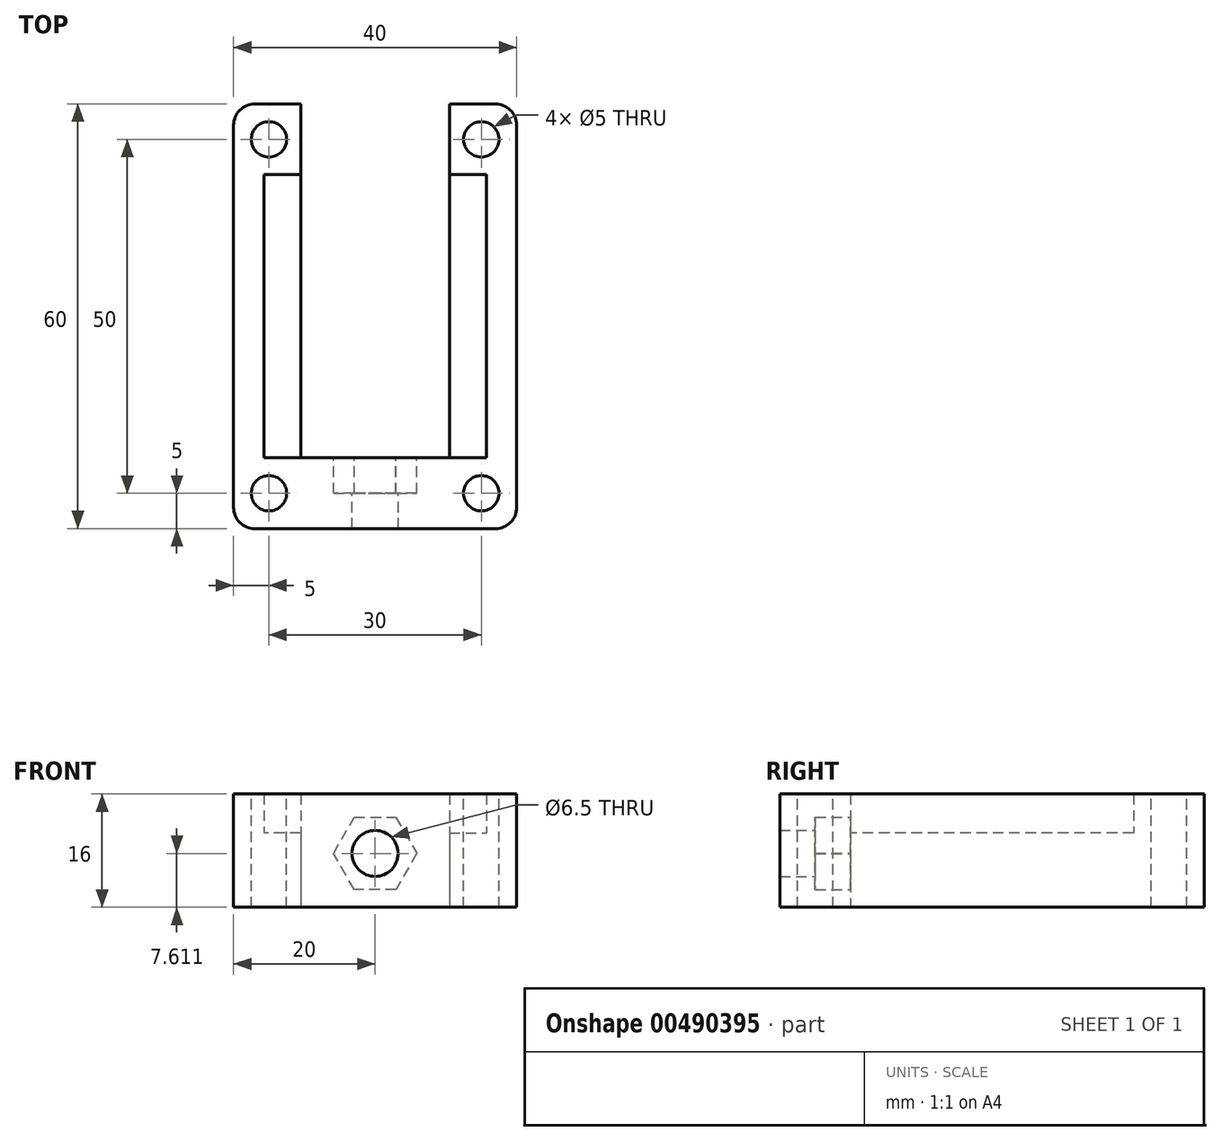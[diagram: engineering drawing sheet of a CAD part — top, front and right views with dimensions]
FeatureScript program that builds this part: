
annotation { "Feature Type Name" : "Feature", "Feature Type Description" : "" }
export const myFeature = defineFeature(function(context is Context, id is Id, definition is map)
    precondition{}
    {
        {
            var Q0;
            Q0=qCreatedBy(makeId("Top.planeOp"),FACE);
            var sketch = newSketch(context, id + "F0", { "sketchPlane" : qUnion([Q0])});
            skLineSegment(sketch, "E0.bottom", {"start": v(20, -30) * mm, "end": v(-20, -30) * mm});
            skLineSegment(sketch, "E0.top", {"start": v(20, 30) * mm, "end": v(-20, 30) * mm});
            skLineSegment(sketch, "E0.left", {"start": v(20, -30) * mm, "end": v(20, 30) * mm});
            skLineSegment(sketch, "E0.right", {"start": v(-20, -30) * mm, "end": v(-20, 30) * mm});
            skPoint(sketch, "E0.middle", {"position": v(0, 0) * mm});
            skLineSegment(sketch, "E1.bottom", {"start": v(10.5, -20) * mm, "end": v(-10.5, -20) * mm});
            skLineSegment(sketch, "E1.top", {"start": v(10.5, 20) * mm, "end": v(-10.5, 20) * mm});
            skLineSegment(sketch, "E1.left", {"start": v(10.5, -20) * mm, "end": v(10.5, 20) * mm});
            skLineSegment(sketch, "E1.right", {"start": v(-10.5, -20) * mm, "end": v(-10.5, 20) * mm});
            skLineSegment(sketch, "E2.bottom", {"start": v(-10.5, 30) * mm, "end": v(-15.7, 30) * mm});
            skLineSegment(sketch, "E2.top", {"start": v(-10.5, -30) * mm, "end": v(-15.7, -30) * mm});
            skLineSegment(sketch, "E2.left", {"start": v(-10.5, 30) * mm, "end": v(-10.5, -30) * mm});
            skLineSegment(sketch, "E2.right", {"start": v(-15.7, 30) * mm, "end": v(-15.7, -30) * mm});
            skLineSegment(sketch, "E3.bottom", {"start": v(10.5, 30) * mm, "end": v(15.7, 30) * mm});
            skLineSegment(sketch, "E3.top", {"start": v(10.5, -30) * mm, "end": v(15.7, -30) * mm});
            skLineSegment(sketch, "E3.left", {"start": v(10.5, 30) * mm, "end": v(10.5, -30) * mm});
            skLineSegment(sketch, "E3.right", {"start": v(15.7, 30) * mm, "end": v(15.7, -30) * mm});
            skLineSegment(sketch, "E4", {"start": v(-10.5, 20) * mm, "end": v(-15.7, 20) * mm});
            skLineSegment(sketch, "E5", {"start": v(-15.7, 20) * mm, "end": v(15.7, 20) * mm});
            skLineSegment(sketch, "E6", {"start": v(10.5, -20) * mm, "end": v(15.7, -20) * mm});
            skLineSegment(sketch, "E7", {"start": v(-10.5, -20) * mm, "end": v(-15.7, -20) * mm});
            skLineSegment(sketch, "E8.bottom", {"start": v(-20, -30) * mm, "end": v(-10, -30) * mm});
            skLineSegment(sketch, "E8.top", {"start": v(-20, -40) * mm, "end": v(-10, -40) * mm});
            skLineSegment(sketch, "E8.left", {"start": v(-20, -30) * mm, "end": v(-20, -40) * mm});
            skLineSegment(sketch, "E8.right", {"start": v(-10, -30) * mm, "end": v(-10, -40) * mm});
            skLineSegment(sketch, "E9.bottom", {"start": v(20, -30) * mm, "end": v(10, -30) * mm});
            skLineSegment(sketch, "E9.top", {"start": v(20, -40) * mm, "end": v(10, -40) * mm});
            skLineSegment(sketch, "E9.left", {"start": v(20, -30) * mm, "end": v(20, -40) * mm});
            skLineSegment(sketch, "E9.right", {"start": v(10, -30) * mm, "end": v(10, -40) * mm});
            skLineSegment(sketch, "E10.bottom", {"start": v(-20, 30) * mm, "end": v(-10, 30) * mm});
            skLineSegment(sketch, "E10.top", {"start": v(-20, 40) * mm, "end": v(-10, 40) * mm});
            skLineSegment(sketch, "E10.left", {"start": v(-20, 30) * mm, "end": v(-20, 40) * mm});
            skLineSegment(sketch, "E10.right", {"start": v(-10, 30) * mm, "end": v(-10, 40) * mm});
            skLineSegment(sketch, "E11.bottom", {"start": v(20, 30) * mm, "end": v(10, 30) * mm});
            skLineSegment(sketch, "E11.top", {"start": v(20, 40) * mm, "end": v(10, 40) * mm});
            skLineSegment(sketch, "E11.left", {"start": v(20, 30) * mm, "end": v(20, 40) * mm});
            skLineSegment(sketch, "E11.right", {"start": v(10, 30) * mm, "end": v(10, 40) * mm});
            skSolve(sketch);
        }
        {
            var Q0;
            {var subQ0=sQuery(id+"F0.wireOp",EDGE,"E2.bottom");Q0=makeQuery(id+"F0.imprint","IMPRINT",FACE,{"disambiguationData":[TD([[makeQuery(id+"F0.imprint","IMPRINT",EDGE,{"derivedFrom":subQ0}),1.0]])]});}
            var Q1;
            {var subQ4=sQuery(id+"F0.wireOp",EDGE,"E0.right");Q1=makeQuery(id+"F0.imprint","IMPRINT",FACE,{"disambiguationData":[TD([[makeQuery(id+"F0.imprint","IMPRINT",EDGE,{"derivedFrom":subQ4}),-1.0]])]});}
            var Q2;
            {var subQ0=sQuery(id+"F0.wireOp",EDGE,"E2.top");Q2=makeQuery(id+"F0.imprint","IMPRINT",FACE,{"disambiguationData":[TD([[makeQuery(id+"F0.imprint","IMPRINT",EDGE,{"derivedFrom":subQ0}),-1.0]])]});}
            var Q3;
            {var subQ5=sQuery(id+"F0.wireOp",EDGE,"E1.bottom");Q3=makeQuery(id+"F0.imprint","IMPRINT",FACE,{"disambiguationData":[TD([[makeQuery(id+"F0.imprint","IMPRINT",EDGE,{"derivedFrom":subQ5}),1.0]])]});}
            var Q4;
            {var subQ0=sQuery(id+"F0.wireOp",EDGE,"E3.top");Q4=makeQuery(id+"F0.imprint","IMPRINT",FACE,{"disambiguationData":[TD([[makeQuery(id+"F0.imprint","IMPRINT",EDGE,{"derivedFrom":subQ0}),1.0]])]});}
            var Q5;
            {var subQ4=sQuery(id+"F0.wireOp",EDGE,"E0.left");Q5=makeQuery(id+"F0.imprint","IMPRINT",FACE,{"disambiguationData":[TD([[makeQuery(id+"F0.imprint","IMPRINT",EDGE,{"derivedFrom":subQ4}),1.0]])]});}
            var Q6;
            {var subQ0=sQuery(id+"F0.wireOp",EDGE,"E3.bottom");Q6=makeQuery(id+"F0.imprint","IMPRINT",FACE,{"disambiguationData":[TD([[makeQuery(id+"F0.imprint","IMPRINT",EDGE,{"derivedFrom":subQ0}),-1.0]])]});}
            var Q7;
            {var subQ0=sQuery(id+"F0.wireOp",EDGE,"E2.left");var subQ5=sQuery(id+"F0.wireOp",EDGE,"E5");var subQ7=makeQuery(id+"F0.imprint","INTERSECT",VERTEX,{"derivedFrom":[subQ0,subQ5]});Q7=makeQuery(id+"F0.imprint","IMPRINT",FACE,{"disambiguationData":[TD([[makeQuery(id+"F0.imprint","IMPRINT",EDGE,{"disambiguationData":[TD([[subQ7,-1.0]])],"derivedFrom":subQ5}),1.0]])]});}
            var Q8;
            {var subQ0=sQuery(id+"F0.wireOp",EDGE,"E6");Q8=makeQuery(id+"F0.imprint","IMPRINT",FACE,{"disambiguationData":[TD([[makeQuery(id+"F0.imprint","IMPRINT",EDGE,{"derivedFrom":subQ0}),-1.0]])]});}
            var Q9;
            {var subQ0=sQuery(id+"F0.wireOp",EDGE,"E7");Q9=makeQuery(id+"F0.imprint","IMPRINT",FACE,{"disambiguationData":[TD([[makeQuery(id+"F0.imprint","IMPRINT",EDGE,{"derivedFrom":subQ0}),1.0]])]});}
            var Q10;
            {var subQ0=sQuery(id+"F0.wireOp",EDGE,"E10.bottom");var subQ1=sQuery(id+"F0.wireOp",EDGE,"E2.left");var subQ2=makeQuery(id+"F0.imprint","INTERSECT",VERTEX,{"derivedFrom":[subQ1,subQ0]});Q10=makeQuery(id+"F0.imprint","IMPRINT",FACE,{"disambiguationData":[TD([[makeQuery(id+"F0.imprint","IMPRINT",EDGE,{"disambiguationData":[TD([[subQ2,-1.0]])],"derivedFrom":subQ1}),-1.0]])]});}
            var Q11;
            {var subQ0=sQuery(id+"F0.wireOp",EDGE,"E11.bottom");var subQ1=sQuery(id+"F0.wireOp",EDGE,"E3.left");var subQ2=makeQuery(id+"F0.imprint","INTERSECT",VERTEX,{"derivedFrom":[subQ1,subQ0]});Q11=makeQuery(id+"F0.imprint","IMPRINT",FACE,{"disambiguationData":[TD([[makeQuery(id+"F0.imprint","IMPRINT",EDGE,{"disambiguationData":[TD([[subQ2,-1.0]])],"derivedFrom":subQ1}),1.0]])]});}
            extrude(context, id + "F1", {"entities" : qUnion([Q0, Q1, Q2, Q3, Q4, Q5, Q6, Q7, Q8, Q9, Q10, Q11]), "depth" : 16 * mm});
        }
        {
            var Q0;
            {var subQ0=sQuery(id+"F0.wireOp",EDGE,"E7");Q0=makeQuery(id+"F0.imprint","IMPRINT",FACE,{"disambiguationData":[TD([[makeQuery(id+"F0.imprint","IMPRINT",EDGE,{"derivedFrom":subQ0}),-1.0]])]});}
            var Q1;
            {var subQ0=sQuery(id+"F0.wireOp",EDGE,"E6");Q1=makeQuery(id+"F0.imprint","IMPRINT",FACE,{"disambiguationData":[TD([[makeQuery(id+"F0.imprint","IMPRINT",EDGE,{"derivedFrom":subQ0}),1.0]])]});}
            extrude(context, id + "F2", {"entities" : qUnion([Q0, Q1]), "operationType" : NewBodyOperationType.ADD, "depth" : 10.5 * mm});
        }
        {
            var Q0;
            Q0=makeQuery(id+"F1.opExtrude","SWEPT_FACE",FACE,{"disambiguationData":[OSD([sQuery(id+"F0.wireOp",EDGE,"E1.bottom"),sQuery(id+"F0.wireOp",EDGE,"E6"),sQuery(id+"F0.wireOp",EDGE,"E7")])]});
            var sketch = newSketch(context, id + "F3", { "sketchPlane" : qUnion([Q0])});
            skCircle(sketch, "E12", {"center": v(0, 7.61) * mm, "radius": 3.25 * mm});
            skPoint(sketch, "E12.centerSnap0", {"position": v(0, 16) * mm});
            skCircle(sketch, "E13.cCircle", {"center": v(0, 7.61) * mm, "radius": 5.1 * mm, "construction": true});
            skLineSegment(sketch, "E13.0", {"start": v(-5.89, 7.63) * mm, "end": v(-2.93, 12.72) * mm});
            skLineSegment(sketch, "E13.1", {"start": v(-2.93, 12.72) * mm, "end": v(2.96, 12.7) * mm});
            skLineSegment(sketch, "E13.2", {"start": v(2.96, 12.7) * mm, "end": v(5.89, 7.6) * mm});
            skLineSegment(sketch, "E13.3", {"start": v(5.89, 7.6) * mm, "end": v(2.93, 2.5) * mm});
            skLineSegment(sketch, "E13.4", {"start": v(2.93, 2.5) * mm, "end": v(-2.96, 2.52) * mm});
            skLineSegment(sketch, "E13.5", {"start": v(-2.96, 2.52) * mm, "end": v(-5.89, 7.63) * mm});
            skPoint(sketch, "E13.0.midPoint", {"position": v(-4.4, 10.18) * mm});
            skSolve(sketch);
        }
        {
            var Q0;
            Q0=makeQuery(id+"F3.imprint","IMPRINT",FACE,{"disambiguationData":[TD([[makeQuery(id+"F3.imprint","IMPRINT",EDGE,{"derivedFrom":sQuery(id+"F3.wireOp",EDGE,"E12")}),1.0]])]});
            extrude(context, id + "F4", {"entities" : qUnion([Q0]), "operationType" : NewBodyOperationType.REMOVE, "oppositeDirection" : true, "depth" : 25 * mm, "hasSecondDirection" : true, "secondDirectionOppositeDirection" : false, "secondDirectionDepth" : 62.6 * mm});
        }
        {
            var Q0;
            Q0=makeQuery(id+"F3.imprint","IMPRINT",FACE,{"disambiguationData":[TD([[makeQuery(id+"F3.imprint","IMPRINT",EDGE,{"derivedFrom":sQuery(id+"F3.wireOp",EDGE,"E12")}),-1.0]])]});
            extrude(context, id + "F5", {"entities" : qUnion([Q0]), "operationType" : NewBodyOperationType.REMOVE, "oppositeDirection" : true, "depth" : 5 * mm, "hasSecondDirection" : true, "secondDirectionOppositeDirection" : false, "secondDirectionDepth" : 45 * mm});
        }
        {
            var Q0;
            Q0=makeQuery(id+"F1.opExtrude","CAP_FACE",FACE,{"disambiguationData":[OSD([sQuery(id+"F0.wireOp",EDGE,"E0.bottom"),sQuery(id+"F0.wireOp",EDGE,"E0.top"),sQuery(id+"F0.wireOp",EDGE,"E0.left"),sQuery(id+"F0.wireOp",EDGE,"E0.right"),sQuery(id+"F0.wireOp",EDGE,"E1.bottom"),sQuery(id+"F0.wireOp",EDGE,"E2.right"),sQuery(id+"F0.wireOp",EDGE,"E3.right"),sQuery(id+"F0.wireOp",EDGE,"E5"),sQuery(id+"F0.wireOp",EDGE,"E6"),sQuery(id+"F0.wireOp",EDGE,"E7"),sQuery(id+"F0.wireOp",EDGE,"E8.bottom"),sQuery(id+"F0.wireOp",EDGE,"E9.bottom"),sQuery(id+"F0.wireOp",EDGE,"E10.bottom"),sQuery(id+"F0.wireOp",EDGE,"E11.bottom")])],"isStart":false});
            var sketch = newSketch(context, id + "F6", { "sketchPlane" : qUnion([Q0])});
            skCircle(sketch, "E14", {"center": v(-15, 25) * mm, "radius": 2.5 * mm});
            skCircle(sketch, "E15.0.1.0", {"center": v(-15, -25) * mm, "radius": 2.5 * mm});
            skCircle(sketch, "E15.1.0.0", {"center": v(15, 25) * mm, "radius": 2.5 * mm});
            skCircle(sketch, "E15.1.1.0", {"center": v(15, -25) * mm, "radius": 2.5 * mm});
            skLineSegment(sketch, "E15.direction1", {"start": v(-15, 25) * mm, "end": v(15, 25) * mm, "construction": true});
            skLineSegment(sketch, "E15.direction2", {"start": v(-15, 25) * mm, "end": v(-15, -25) * mm, "construction": true});
            skSolve(sketch);
        }
        {
            var Q0;
            Q0=makeQuery(id+"F6.imprint","IMPRINT",FACE,{"disambiguationData":[TD([[makeQuery(id+"F6.imprint","IMPRINT",EDGE,{"derivedFrom":sQuery(id+"F6.wireOp",EDGE,"E15.0.1.0")}),1.0]])]});
            var Q1;
            Q1=makeQuery(id+"F6.imprint","IMPRINT",FACE,{"disambiguationData":[TD([[makeQuery(id+"F6.imprint","IMPRINT",EDGE,{"derivedFrom":sQuery(id+"F6.wireOp",EDGE,"E15.1.1.0")}),1.0]])]});
            var Q2;
            Q2=makeQuery(id+"F6.imprint","IMPRINT",FACE,{"disambiguationData":[TD([[makeQuery(id+"F6.imprint","IMPRINT",EDGE,{"derivedFrom":sQuery(id+"F6.wireOp",EDGE,"E15.1.0.0")}),1.0]])]});
            var Q3;
            Q3=makeQuery(id+"F6.imprint","IMPRINT",FACE,{"disambiguationData":[TD([[makeQuery(id+"F6.imprint","IMPRINT",EDGE,{"derivedFrom":sQuery(id+"F6.wireOp",EDGE,"E14")}),1.0]])]});
            extrude(context, id + "F7", {"entities" : qUnion([Q0, Q1, Q2, Q3]), "operationType" : NewBodyOperationType.REMOVE, "oppositeDirection" : true, "depth" : 20 * mm});
        }
        {
            var Q0;
            Q0=makeQuery(id+"F1.opExtrude","SWEPT_EDGE",EDGE,{"disambiguationData":[OSD([sQuery(id+"F0.wireOp",EDGE,"E0.left"),sQuery(id+"F0.wireOp",EDGE,"E9.bottom"),sQuery(id+"F0.wireOp",EDGE,"E9.left")])]});
            var Q1;
            Q1=makeQuery(id+"F1.opExtrude","SWEPT_EDGE",EDGE,{"disambiguationData":[OSD([sQuery(id+"F0.wireOp",EDGE,"E0.left"),sQuery(id+"F0.wireOp",EDGE,"E11.bottom"),sQuery(id+"F0.wireOp",EDGE,"E11.left")])]});
            var Q2;
            Q2=makeQuery(id+"F1.opExtrude","SWEPT_EDGE",EDGE,{"disambiguationData":[OSD([sQuery(id+"F0.wireOp",EDGE,"E0.right"),sQuery(id+"F0.wireOp",EDGE,"E10.bottom"),sQuery(id+"F0.wireOp",EDGE,"E10.left")])]});
            var Q3;
            Q3=makeQuery(id+"F1.opExtrude","SWEPT_EDGE",EDGE,{"disambiguationData":[OSD([sQuery(id+"F0.wireOp",EDGE,"E0.right"),sQuery(id+"F0.wireOp",EDGE,"E8.bottom"),sQuery(id+"F0.wireOp",EDGE,"E8.left")])]});
            fillet(context, id + "F8", {"entities" : qUnion([Q0, Q1, Q2, Q3]), "radius" : 3 * mm, "tangentPropagation" : true, "allowEdgeOverflow" : false});
        }
    });
